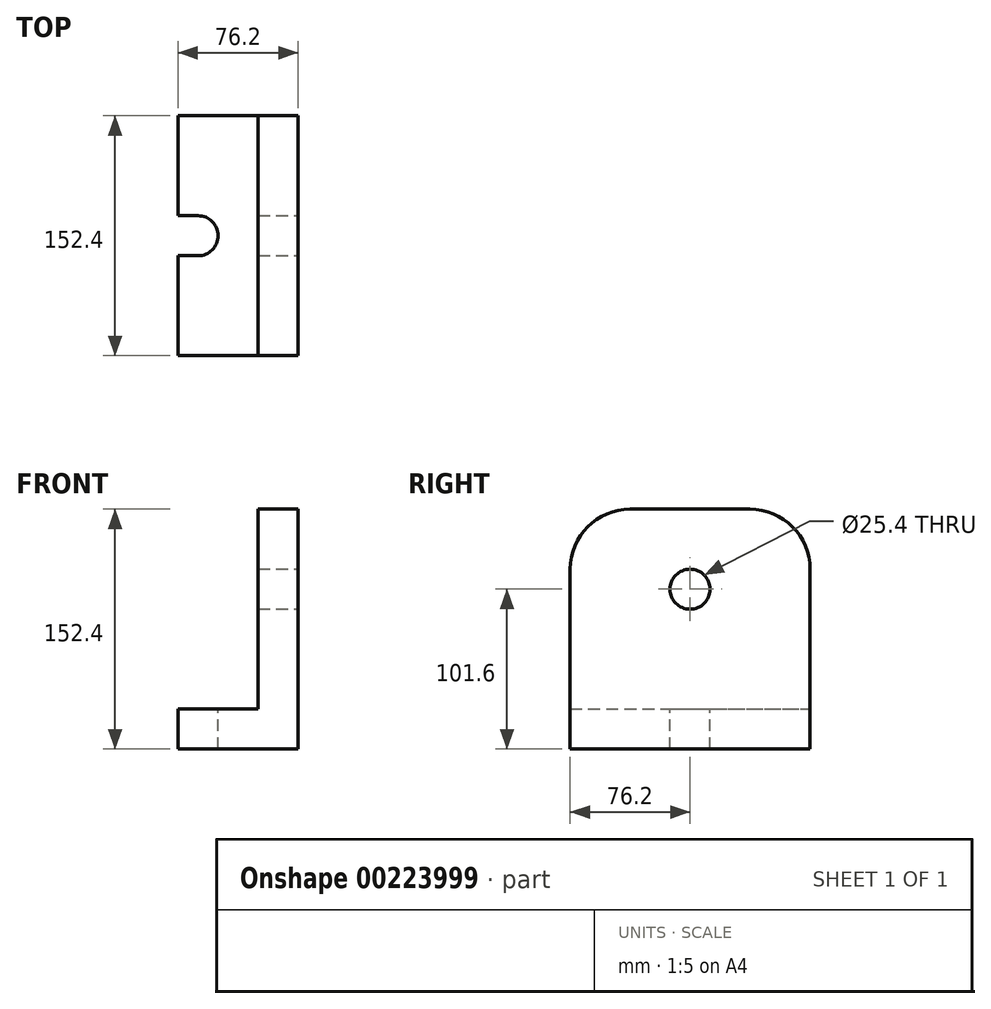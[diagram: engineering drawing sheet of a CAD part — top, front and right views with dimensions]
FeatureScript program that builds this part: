
annotation { "Feature Type Name" : "Feature", "Feature Type Description" : "" }
export const myFeature = defineFeature(function(context is Context, id is Id, definition is map)
    precondition{}
    {
        {
            var Q0;
            Q0=qCreatedBy(makeId("Front.planeOp"),FACE);
            var sketch = newSketch(context, id + "F0", { "sketchPlane" : qUnion([Q0])});
            skLineSegment(sketch, "E0", {"start": v(0, 0) * mm, "end": v(0, 152.4) * mm});
            skLineSegment(sketch, "E1", {"start": v(0, 0) * mm, "end": v(-76.2, 0) * mm});
            skLineSegment(sketch, "E2", {"start": v(-76.2, 0) * mm, "end": v(-76.2, 25.4) * mm});
            skLineSegment(sketch, "E3", {"start": v(0, 152.4) * mm, "end": v(-25.4, 152.4) * mm});
            skLineSegment(sketch, "E4", {"start": v(-25.4, 152.4) * mm, "end": v(-25.4, 25.4) * mm});
            skLineSegment(sketch, "E5", {"start": v(-76.2, 25.4) * mm, "end": v(-25.4, 25.4) * mm});
            skSolve(sketch);
        }
        {
            var Q0;
            Q0=makeQuery(id+"F0.imprint","IMPRINT",FACE,{"disambiguationData":[TD([[makeQuery(id+"F0.imprint","IMPRINT",EDGE,{"derivedFrom":sQuery(id+"F0.wireOp",EDGE,"E0")}),1.0]])]});
            extrude(context, id + "F1", {"entities" : qUnion([Q0]), "depth" : 76.2 * mm, "hasSecondDirection" : true, "secondDirectionOppositeDirection" : true, "secondDirectionDepth" : 76.2 * mm});
        }
        {
            var Q0;
            Q0=makeQuery(id+"F1.opExtrude","SWEPT_FACE",FACE,{"disambiguationData":[OSD([sQuery(id+"F0.wireOp",EDGE,"E0")])]});
            var sketch = newSketch(context, id + "F2", { "sketchPlane" : qUnion([Q0])});
            skCircle(sketch, "E6", {"center": v(0, 101.6) * mm, "radius": 12.7 * mm});
            skPoint(sketch, "E6.centerSnap0", {"position": v(0, 152.4) * mm});
            skSolve(sketch);
        }
        {
            var Q0;
            Q0=makeQuery(id+"F2.imprint","IMPRINT",FACE,{"disambiguationData":[TD([[makeQuery(id+"F2.imprint","IMPRINT",EDGE,{"derivedFrom":sQuery(id+"F2.wireOp",EDGE,"E6")}),1.0]])]});
            extrude(context, id + "F3", {"entities" : qUnion([Q0]), "operationType" : NewBodyOperationType.REMOVE, "endBound" : BoundingType.THROUGH_ALL, "oppositeDirection" : true, "depth" : 25.4 * mm});
        }
        {
            var Q0;
            Q0=makeQuery(id+"F1.opExtrude","SWEPT_FACE",FACE,{"disambiguationData":[OSD([sQuery(id+"F0.wireOp",EDGE,"E5")])]});
            var sketch = newSketch(context, id + "F4", { "sketchPlane" : qUnion([Q0])});
            skLineSegment(sketch, "E7", {"start": v(-76.2, 12.7) * mm, "end": v(-63.5, 12.7) * mm});
            skLineSegment(sketch, "E8", {"start": v(-76.2, -12.7) * mm, "end": v(-63.5, -12.7) * mm});
            skArc(sketch, "E9", {"start": v(-63.5, -12.7) * mm, "mid": v(-50.8, 0) * mm, "end": v(-63.5, 12.7) * mm});
            skSolve(sketch);
        }
        {
            var Q0;
            {var subQ0=sQuery(id+"F4.wireOp",EDGE,"E7");Q0=makeQuery(id+"F4.imprint","IMPRINT",FACE,{"disambiguationData":[TD([[makeQuery(id+"F4.imprint","IMPRINT",EDGE,{"derivedFrom":subQ0}),-1.0]])]});}
            extrude(context, id + "F5", {"entities" : qUnion([Q0]), "operationType" : NewBodyOperationType.REMOVE, "endBound" : BoundingType.THROUGH_ALL, "oppositeDirection" : true, "depth" : 25.4 * mm});
        }
        {
            var Q0;
            Q0=makeQuery(id+"F1.opExtrude","CAP_EDGE",EDGE,{"disambiguationData":[OSD([sQuery(id+"F0.wireOp",EDGE,"E3")])],"isStart":false});
            fillet(context, id + "F6", {"entities" : qUnion([Q0]), "radius" : 38.1 * mm, "tangentPropagation" : true, "allowEdgeOverflow" : false});
        }
        {
            var Q0;
            Q0=makeQuery(id+"F1.opExtrude","CAP_EDGE",EDGE,{"disambiguationData":[OSD([sQuery(id+"F0.wireOp",EDGE,"E3")])],"isStart":true});
            fillet(context, id + "F7", {"entities" : qUnion([Q0]), "radius" : 38.1 * mm, "tangentPropagation" : true, "allowEdgeOverflow" : false});
        }
    });
